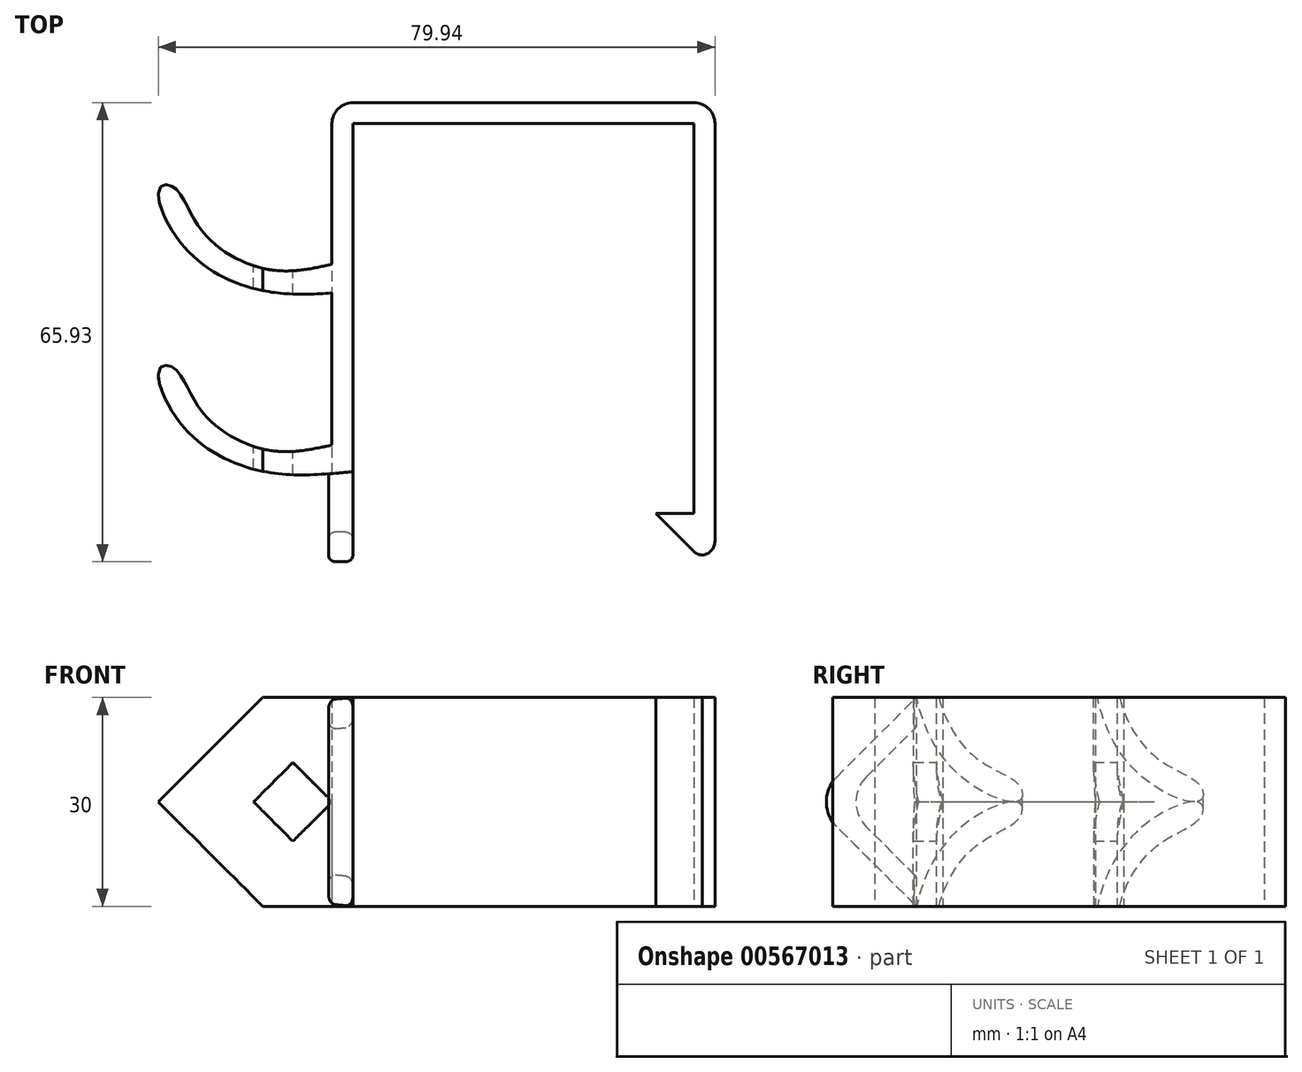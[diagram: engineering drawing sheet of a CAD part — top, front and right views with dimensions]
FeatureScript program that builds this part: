
annotation { "Feature Type Name" : "Feature", "Feature Type Description" : "" }
export const myFeature = defineFeature(function(context is Context, id is Id, definition is map)
    precondition{}
    {
        {
            var Q0;
            Q0=qCreatedBy(makeId("Top.planeOp"),FACE);
            var sketch = newSketch(context, id + "F0", { "sketchPlane" : qUnion([Q0])});
            skLineSegment(sketch, "E0", {"start": v(6.57, -20.82) * mm, "end": v(12.07, -20.82) * mm});
            skLineSegment(sketch, "E1", {"start": v(12.07, -20.82) * mm, "end": v(12.07, 35.18) * mm});
            skLineSegment(sketch, "E2", {"start": v(12.07, 35.18) * mm, "end": v(-36.93, 35.18) * mm});
            skLineSegment(sketch, "E3", {"start": v(-36.93, 35.18) * mm, "end": v(-36.93, -14.82) * mm});
            skLineSegment(sketch, "E4", {"start": v(6.57, -20.82) * mm, "end": v(12.57, -26.82) * mm});
            skLineSegment(sketch, "E5", {"start": v(12.57, -26.82) * mm, "end": v(15.07, -26.82) * mm});
            skLineSegment(sketch, "E6", {"start": v(15.07, -26.82) * mm, "end": v(15.07, 38.18) * mm});
            skLineSegment(sketch, "E7", {"start": v(15.07, 38.18) * mm, "end": v(-39.93, 38.18) * mm});
            skLineSegment(sketch, "E8", {"start": v(-39.93, 38.18) * mm, "end": v(-39.93, -13.14) * mm});
            skLineSegment(sketch, "E9", {"start": v(-39.93, -13.14) * mm, "end": v(-36.93, -14.82) * mm});
            skFitSpline(sketch, "E10", {"points": [v(-36.93, -14.82) * mm, v(-49.6, -14.82) * mm, v(-61.45, -8.15) * mm, v(-64.66, 0) * mm, v(-62.56, 0) * mm, v(-58.61, -6.18) * mm, v(-49.1, -11.73) * mm, v(-39.93, -11) * mm], "startDerivative": vector(-73.6, -7.07) * mm, "endDerivative": vector(61.06, 13.43) * mm});
            skLineSegment(sketch, "E11", {"start": v(-39.93, 12.81) * mm, "end": v(-36.93, 11.13) * mm});
            skFitSpline(sketch, "E12", {"points": [v(-36.93, 11.13) * mm, v(-49.6, 11.13) * mm, v(-61.45, 17.8) * mm, v(-64.66, 25.95) * mm, v(-62.56, 25.95) * mm, v(-58.61, 19.78) * mm, v(-49.1, 14.22) * mm, v(-39.93, 14.96) * mm], "startDerivative": vector(-73.6, -7.07) * mm, "endDerivative": vector(61.06, 13.43) * mm});
            skSolve(sketch);
        }
        {
            var Q0;
            Q0 = qSketchRegion(id + "F0", true);
            extrude(context, id + "F1", {"entities" : qUnion([Q0]), "depth" : 30 * mm, "offsetDistance" : 25 * mm});
        }
        {
            var Q0;
            Q0=qCreatedBy(makeId("Front.planeOp"),FACE);
            var sketch = newSketch(context, id + "F2", { "sketchPlane" : qUnion([Q0])});
            skLineSegment(sketch, "E13", {"start": v(-38.37, 0) * mm, "end": v(-38.37, 30) * mm, "construction": true});
            skLineSegment(sketch, "E14", {"start": v(-38.37, 30) * mm, "end": v(-38.37, 15) * mm, "construction": true});
            skLineSegment(sketch, "E15", {"start": v(-38.37, 15) * mm, "end": v(-64.95, 15) * mm, "construction": true});
            skLineSegment(sketch, "E16", {"start": v(-64.47, 23.7) * mm, "end": v(-55.77, 15) * mm});
            skLineSegment(sketch, "E17", {"start": v(-64.47, 23.7) * mm, "end": v(-65.46, 24.75) * mm});
            skLineSegment(sketch, "E18", {"start": v(-65.46, 24.75) * mm, "end": v(-57.35, 32.86) * mm});
            skLineSegment(sketch, "E19.MirrorCS", {"start": v(-64.47, 6.3) * mm, "end": v(-65.46, 5.25) * mm});
            skLineSegment(sketch, "E20.MirrorCS", {"start": v(-64.47, 6.3) * mm, "end": v(-55.77, 15) * mm});
            skLineSegment(sketch, "E21.MirrorCS", {"start": v(-65.46, 5.25) * mm, "end": v(-57.35, -2.86) * mm});
            skLineSegment(sketch, "E22", {"start": v(-57.35, -2.86) * mm, "end": v(-67.44, -2.86) * mm});
            skLineSegment(sketch, "E23", {"start": v(-67.44, -2.86) * mm, "end": v(-67.44, 34.81) * mm});
            skLineSegment(sketch, "E24", {"start": v(-67.44, 34.81) * mm, "end": v(-57.35, 32.86) * mm});
            skSolve(sketch);
        }
        {
            var Q0;
            Q0=makeQuery(id+"F1.opExtrude","SWEPT_FACE",FACE,{"disambiguationData":[OSD([sQuery(id+"F0.wireOp",EDGE,"E3")])]});
            var sketch = newSketch(context, id + "F3", { "sketchPlane" : qUnion([Q0])});
            skLineSegment(sketch, "E25", {"start": v(-14.82, 0) * mm, "end": v(-29.82, 15) * mm});
            skPoint(sketch, "E25.endSnap0", {"position": v(-14.82, 15) * mm});
            skLineSegment(sketch, "E26", {"start": v(-29.82, 15) * mm, "end": v(-14.82, 30) * mm});
            skLineSegment(sketch, "E27.0", {"start": v(-25.58, 15) * mm, "end": v(-12.7, 27.88) * mm});
            skLineSegment(sketch, "E27.1", {"start": v(-12.7, 2.12) * mm, "end": v(-25.58, 15) * mm});
            skLineSegment(sketch, "E28", {"start": v(-14.82, 0) * mm, "end": v(-12.7, 2.12) * mm});
            skLineSegment(sketch, "E29", {"start": v(-12.7, 27.88) * mm, "end": v(-14.82, 30) * mm});
            skSolve(sketch);
        }
        {
            var Q0;
            Q0 = qSketchRegion(id + "F3", true);
            extrude(context, id + "F4", {"entities" : qUnion([Q0]), "operationType" : NewBodyOperationType.ADD, "oppositeDirection" : true, "depth" : 3.5 * mm, "offsetDistance" : 25 * mm});
        }
        {
            var Q0;
            Q0=makeQuery(id+"F4.opExtrude","SWEPT_EDGE",EDGE,{"disambiguationData":[OSD([sQuery(id+"F3.wireOp",EDGE,"E25"),sQuery(id+"F3.wireOp",EDGE,"E26")])]});
            var Q1;
            Q1=makeQuery(id+"F4.opExtrude","SWEPT_EDGE",EDGE,{"disambiguationData":[OSD([sQuery(id+"F3.wireOp",EDGE,"E27.0"),sQuery(id+"F3.wireOp",EDGE,"E27.1")])]});
            fillet(context, id + "F5", {"entities" : qUnion([Q0, Q1]), "radius" : 5 * mm, "tangentPropagation" : true, "allowEdgeOverflow" : false});
        }
        {
            var Q0;
            Q0=makeQuery(id+"F4.opExtrude","CAP_EDGE",EDGE,{"disambiguationData":[OSD([sQuery(id+"F3.wireOp",EDGE,"E27.1")])],"isStart":true});
            var Q1;
            Q1=makeQuery(id+"F4.opExtrude","CAP_EDGE",EDGE,{"disambiguationData":[OSD([sQuery(id+"F3.wireOp",EDGE,"E27.0")])],"isStart":false});
            fillet(context, id + "F6", {"entities" : qUnion([Q0, Q1]), "radius" : 1 * mm, "tangentPropagation" : true, "allowEdgeOverflow" : false});
        }
        {
            var Q0;
            Q0=makeQuery(id+"F4.opExtrude","CAP_EDGE",EDGE,{"disambiguationData":[OSD([sQuery(id+"F3.wireOp",EDGE,"E25")])],"isStart":false});
            var Q1;
            Q1=makeQuery(id+"F4.opExtrude","CAP_EDGE",EDGE,{"disambiguationData":[OSD([sQuery(id+"F3.wireOp",EDGE,"E25")])],"isStart":true});
            fillet(context, id + "F7", {"entities" : qUnion([Q0, Q1]), "radius" : 1 * mm, "tangentPropagation" : true, "allowEdgeOverflow" : false});
        }
        {
            var Q0;
            Q0=makeQuery(id+"F1.opExtrude","SWEPT_EDGE",EDGE,{"disambiguationData":[OSD([sQuery(id+"F0.wireOp",EDGE,"E7"),sQuery(id+"F0.wireOp",EDGE,"E8")])]});
            var Q1;
            Q1=makeQuery(id+"F1.opExtrude","SWEPT_EDGE",EDGE,{"disambiguationData":[OSD([sQuery(id+"F0.wireOp",EDGE,"E6"),sQuery(id+"F0.wireOp",EDGE,"E7")])]});
            fillet(context, id + "F8", {"entities" : qUnion([Q0, Q1]), "radius" : 3 * mm, "tangentPropagation" : true, "allowEdgeOverflow" : false});
        }
        {
            var Q0;
            Q0=makeQuery(id+"F1.opExtrude","SWEPT_EDGE",EDGE,{"disambiguationData":[OSD([sQuery(id+"F0.wireOp",EDGE,"E5"),sQuery(id+"F0.wireOp",EDGE,"E6")])]});
            var Q1;
            Q1=makeQuery(id+"F1.opExtrude","SWEPT_EDGE",EDGE,{"disambiguationData":[OSD([sQuery(id+"F0.wireOp",EDGE,"E4"),sQuery(id+"F0.wireOp",EDGE,"E5")])]});
            fillet(context, id + "F9", {"entities" : qUnion([Q0, Q1]), "radius" : 2 * mm, "tangentPropagation" : true, "allowEdgeOverflow" : false});
        }
        {
            var Q0;
            Q0=qCreatedBy(makeId("Front.planeOp"),FACE);
            var sketch = newSketch(context, id + "F10", { "sketchPlane" : qUnion([Q0])});
            skLineSegment(sketch, "E30", {"start": v(-64.87, 0) * mm, "end": v(-64.87, 30) * mm, "construction": true});
            skLineSegment(sketch, "E31", {"start": v(-64.87, 15) * mm, "end": v(-44.46, 35.4) * mm});
            skLineSegment(sketch, "E32", {"start": v(-64.87, 15) * mm, "end": v(-45.15, -4.72) * mm});
            skLineSegment(sketch, "E33", {"start": v(-64.87, 15) * mm, "end": v(-64.87, 47.2) * mm});
            skLineSegment(sketch, "E34", {"start": v(-64.87, 47.2) * mm, "end": v(-44.46, 35.4) * mm});
            skLineSegment(sketch, "E35", {"start": v(-64.87, 15) * mm, "end": v(-64.87, -17.9) * mm});
            skLineSegment(sketch, "E36", {"start": v(-64.87, -17.9) * mm, "end": v(-45.15, -4.72) * mm});
            skArc(sketch, "E37", {"start": v(-64.87, 47.2) * mm, "mid": v(-96.19, 14.65) * mm, "end": v(-64.87, -17.9) * mm});
            skSolve(sketch);
        }
        {
            var Q0;
            Q0 = qSketchRegion(id + "F10", true);
            extrude(context, id + "F11", {"entities" : qUnion([Q0]), "operationType" : NewBodyOperationType.REMOVE, "endBound" : BoundingType.SYMMETRIC, "oppositeDirection" : true, "depth" : 81.8 * mm, "offsetDistance" : 25 * mm});
        }
        {
            var Q0;
            Q0=qCreatedBy(makeId("Front.planeOp"),FACE);
            var sketch = newSketch(context, id + "F12", { "sketchPlane" : qUnion([Q0])});
            skLineSegment(sketch, "E38", {"start": v(-39.88, 15) * mm, "end": v(-45.53, 20.66) * mm});
            skLineSegment(sketch, "E39", {"start": v(-45.53, 20.66) * mm, "end": v(-51.19, 15) * mm});
            skLineSegment(sketch, "E40", {"start": v(-51.19, 15) * mm, "end": v(-45.53, 9.34) * mm});
            skLineSegment(sketch, "E41", {"start": v(-45.53, 9.34) * mm, "end": v(-39.88, 15) * mm});
            skSolve(sketch);
        }
        {
            var Q0;
            Q0 = qSketchRegion(id + "F12", true);
            extrude(context, id + "F13", {"entities" : qUnion([Q0]), "operationType" : NewBodyOperationType.REMOVE, "endBound" : BoundingType.SYMMETRIC, "depth" : 38.6 * mm, "offsetDistance" : 25 * mm});
        }
    });
